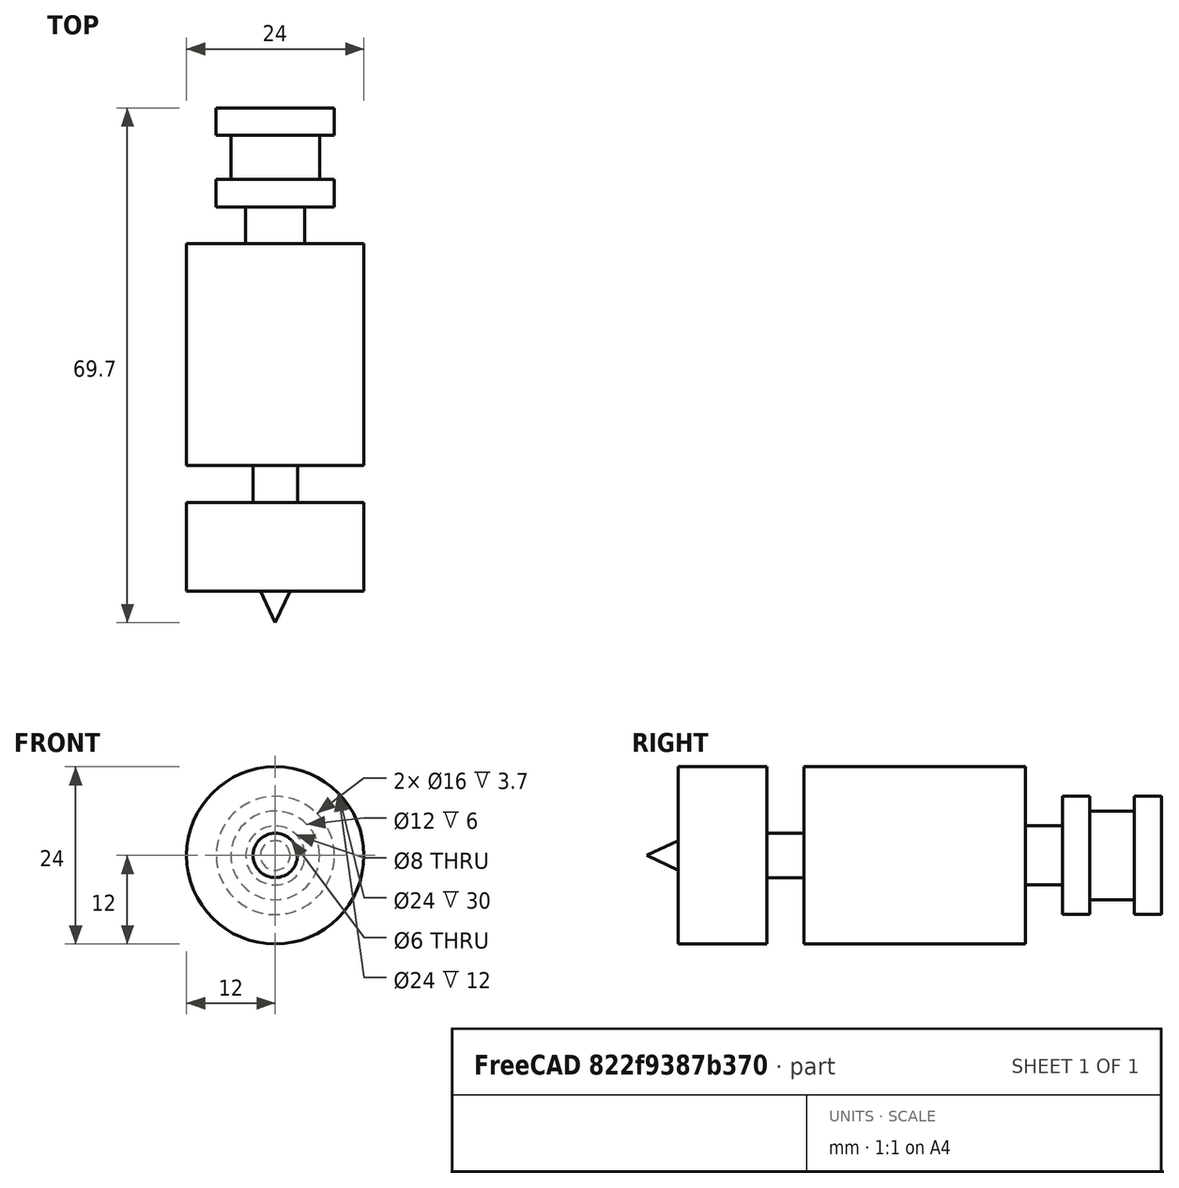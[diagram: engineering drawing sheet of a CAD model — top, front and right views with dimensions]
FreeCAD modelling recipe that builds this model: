
FCSTD DOCUMENT  (FreeCAD 0.16RUnknown)
Label: e3d-v6
License: All rights reserved
LicenseURL: http://en.wikipedia.org/wiki/All_rights_reserved
objects: Sketcher::SketchObject×1, Part::Revolution×1
note: 2 computed .brp shape members not serialized (recipe doc carries the construction recipe); baked Part::Feature solids carry a one-line shape summary decoded from their .brp

FEATURE [Sketcher::SketchObject] Sketch
  sketch-geometry (16):
    g0: LineSegment StartX=0 StartY=34.85 StartZ=0 EndX=-8 EndY=34.85 EndZ=0
    g1: LineSegment StartX=-8 StartY=34.85 StartZ=0 EndX=-8 EndY=31.15 EndZ=0
    g2: LineSegment StartX=-8 StartY=31.15 StartZ=0 EndX=-6 EndY=31.15 EndZ=0
    g3: LineSegment StartX=-6 StartY=31.15 StartZ=0 EndX=-6 EndY=25.15 EndZ=0
    g4: LineSegment StartX=-6 StartY=25.15 StartZ=0 EndX=-8 EndY=25.15 EndZ=0
    g5: LineSegment StartX=-8 StartY=25.15 StartZ=0 EndX=-8 EndY=21.45 EndZ=0
    g6: LineSegment StartX=-8 StartY=21.45 StartZ=0 EndX=-4 EndY=21.45 EndZ=0
    g7: LineSegment StartX=-4 StartY=21.45 StartZ=0 EndX=-4 EndY=16.45 EndZ=0
    g8: LineSegment StartX=-4 StartY=16.45 StartZ=0 EndX=-12 EndY=16.45 EndZ=0
    g9: LineSegment StartX=-12 StartY=16.45 StartZ=0 EndX=-12 EndY=-13.55 EndZ=0
    g10: LineSegment StartX=-12 StartY=-13.55 StartZ=0 EndX=-3 EndY=-13.55 EndZ=0
    g11: LineSegment StartX=-3 StartY=-13.55 StartZ=0 EndX=-3 EndY=-18.55 EndZ=0
    g12: LineSegment StartX=-3 StartY=-18.55 StartZ=0 EndX=-12 EndY=-18.55 EndZ=0
    g13: LineSegment StartX=-12 StartY=-18.55 StartZ=0 EndX=-12 EndY=-30.55 EndZ=0
    g14: LineSegment StartX=-12 StartY=-30.55 StartZ=0 EndX=-2 EndY=-30.55 EndZ=0
    g15: LineSegment StartX=-2 StartY=-30.55 StartZ=0 EndX=0 EndY=-34.85 EndZ=0
  constraints (49):
    c: Horizontal(g0)
    c: Coincident(g0,g1)
    c: Coincident(g1,g2)
    c: Horizontal(g2)
    c: Coincident(g2,g3)
    c: Vertical(g3)
    c: Coincident(g3,g4)
    c: Coincident(g4,g5)
    c: Coincident(g5,g6)
    c: Horizontal(g6)
    c: Coincident(g6,g7)
    c: Coincident(g7,g8)
    c: Horizontal(g8)
    c: Coincident(g8,g9)
    c: Vertical(g9)
    c: Coincident(g9,g10)
    c: Horizontal(g10)
    c: Coincident(g10,g11)
    c: Vertical(g11)
    c: Vertical(g7)
    c: Vertical(g5)
    c: Horizontal(g4)
    c: Vertical(g1)
    c: Coincident(g11,g12)
    c: Horizontal(g12)
    c: Coincident(g12,g13)
    c: Vertical(g13)
    c: Coincident(g13,g14)
    c: Horizontal(g14)
    c: Coincident(g14,g15)
    c: PointOnObject(g15,g-2)
    c: DistanceY(g1,g1) = 3.7
    c: Equal(g5,g1)
    c: DistanceY(g3,g3) = 6
    c: DistanceX(g8,g-1) = 12
    c: DistanceX(g0,g0) = 8
    c: Equal(g2,g4)
    c: DistanceY(g15,g0) = 69.7
    c: DistanceX(g0,g-1) = 0
    c: DistanceY(g13,g13) = 12
    c: DistanceX(g12,g9) = 0
    c: DistanceX(g10,g10) = 9
    c: DistanceY(g11,g11) = 5
    c: DistanceY(g7,g7) = 5
    c: DistanceX(g6,g-1) = 4
    c: DistanceY(g9,g9) = 30
    c: DistanceY(g-1,g0) = 34.85
    c: DistanceX(g14,g14) = 10
    c: DistanceX(g2,g-1) = 6
FEATURE [Part::Revolution] Revolve
  Angle = 360
  Axis = (0,1,0)
  Base = (0,0,0)
  Solid = false
  Source = -> Sketch
